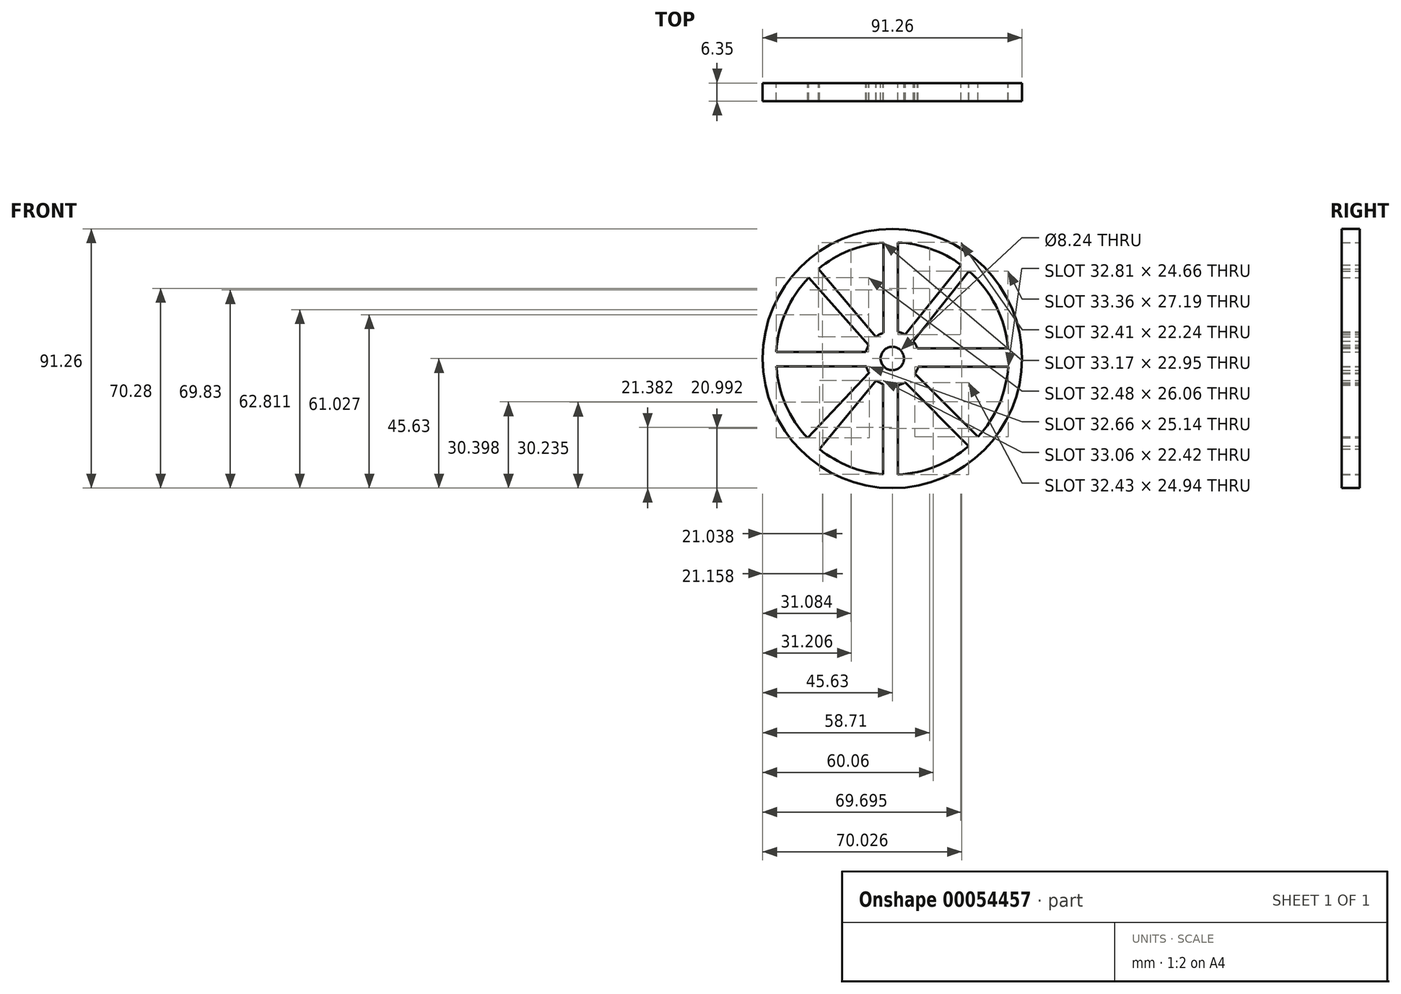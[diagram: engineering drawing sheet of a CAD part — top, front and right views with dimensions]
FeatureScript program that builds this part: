
annotation { "Feature Type Name" : "Feature", "Feature Type Description" : "" }
export const myFeature = defineFeature(function(context is Context, id is Id, definition is map)
    precondition{}
    {
        {
            var Q0;
            Q0=qCreatedBy(makeId("Front.planeOp"),FACE);
            var sketch = newSketch(context, id + "F0", { "sketchPlane" : qUnion([Q0])});
            skCircle(sketch, "E0", {"center": v(0, 0) * mm, "radius": 9.58 * mm});
            skCircle(sketch, "E1", {"center": v(0, 0) * mm, "radius": 40.9 * mm});
            skCircle(sketch, "E2", {"center": v(0, 0) * mm, "radius": 45.63 * mm});
            skLineSegment(sketch, "E3", {"start": v(-40.83, 2.36) * mm, "end": v(-9.28, 2.36) * mm});
            skLineSegment(sketch, "E4", {"start": v(8.88, 3.58) * mm, "end": v(40.74, 3.58) * mm});
            skLineSegment(sketch, "E5", {"start": v(9.13, -2.9) * mm, "end": v(40.8, -2.9) * mm});
            skLineSegment(sketch, "E6", {"start": v(-3.07, 9.07) * mm, "end": v(-3.07, 40.79) * mm});
            skLineSegment(sketch, "E7", {"start": v(1.96, 9.38) * mm, "end": v(1.96, 40.85) * mm});
            skLineSegment(sketch, "E8", {"start": v(-3.21, -9.02) * mm, "end": v(-3.21, -40.78) * mm});
            skLineSegment(sketch, "E9", {"start": v(1.96, -9.38) * mm, "end": v(1.96, -40.85) * mm});
            skLineSegment(sketch, "E10", {"start": v(-9.15, -2.82) * mm, "end": v(-40.8, -2.82) * mm});
            skLineSegment(sketch, "E11", {"start": v(-5.81, 7.61) * mm, "end": v(-26.02, 31.56) * mm});
            skLineSegment(sketch, "E12", {"start": v(-8.35, 4.7) * mm, "end": v(-29.4, 28.43) * mm});
            skLineSegment(sketch, "E13", {"start": v(4.52, 8.44) * mm, "end": v(24.2, 32.97) * mm});
            skLineSegment(sketch, "E14", {"start": v(7.38, 6.1) * mm, "end": v(26.94, 30.78) * mm});
            skLineSegment(sketch, "E15", {"start": v(8, -5.28) * mm, "end": v(30.22, -27.56) * mm});
            skLineSegment(sketch, "E16", {"start": v(4.56, -8.42) * mm, "end": v(26.9, -30.81) * mm});
            skLineSegment(sketch, "E17", {"start": v(-8.14, -5.05) * mm, "end": v(-29.85, -27.97) * mm});
            skLineSegment(sketch, "E18", {"start": v(-5.67, -7.72) * mm, "end": v(-25.64, -31.87) * mm});
            skCircle(sketch, "E19", {"center": v(0, 0) * mm, "radius": 4.12 * mm});
            skSolve(sketch);
        }
        {
            var Q0;
            Q0=makeQuery(id+"F0.imprint","IMPRINT",FACE,{"disambiguationData":[TD([[makeQuery(id+"F0.imprint","IMPRINT",EDGE,{"derivedFrom":sQuery(id+"F0.wireOp",EDGE,"E19")}),-1.0]])]});
            var Q1;
            {var subQ0=sQuery(id+"F0.wireOp",EDGE,"E6");Q1=makeQuery(id+"F0.imprint","IMPRINT",FACE,{"disambiguationData":[TD([[makeQuery(id+"F0.imprint","IMPRINT",EDGE,{"derivedFrom":subQ0}),-1.0]])]});}
            var Q2;
            {var subQ0=sQuery(id+"F0.wireOp",EDGE,"E11");Q2=makeQuery(id+"F0.imprint","IMPRINT",FACE,{"disambiguationData":[TD([[makeQuery(id+"F0.imprint","IMPRINT",EDGE,{"derivedFrom":subQ0}),1.0]])]});}
            var Q3;
            {var subQ0=sQuery(id+"F0.wireOp",EDGE,"E3");Q3=makeQuery(id+"F0.imprint","IMPRINT",FACE,{"disambiguationData":[TD([[makeQuery(id+"F0.imprint","IMPRINT",EDGE,{"derivedFrom":subQ0}),-1.0]])]});}
            var Q4;
            {var subQ0=sQuery(id+"F0.wireOp",EDGE,"E17");Q4=makeQuery(id+"F0.imprint","IMPRINT",FACE,{"disambiguationData":[TD([[makeQuery(id+"F0.imprint","IMPRINT",EDGE,{"derivedFrom":subQ0}),1.0]])]});}
            var Q5;
            {var subQ0=sQuery(id+"F0.wireOp",EDGE,"E8");Q5=makeQuery(id+"F0.imprint","IMPRINT",FACE,{"disambiguationData":[TD([[makeQuery(id+"F0.imprint","IMPRINT",EDGE,{"derivedFrom":subQ0}),1.0]])]});}
            var Q6;
            {var subQ0=sQuery(id+"F0.wireOp",EDGE,"E15");Q6=makeQuery(id+"F0.imprint","IMPRINT",FACE,{"disambiguationData":[TD([[makeQuery(id+"F0.imprint","IMPRINT",EDGE,{"derivedFrom":subQ0}),-1.0]])]});}
            var Q7;
            {var subQ0=sQuery(id+"F0.wireOp",EDGE,"E4");Q7=makeQuery(id+"F0.imprint","IMPRINT",FACE,{"disambiguationData":[TD([[makeQuery(id+"F0.imprint","IMPRINT",EDGE,{"derivedFrom":subQ0}),-1.0]])]});}
            var Q8;
            {var subQ0=sQuery(id+"F0.wireOp",EDGE,"E13");Q8=makeQuery(id+"F0.imprint","IMPRINT",FACE,{"disambiguationData":[TD([[makeQuery(id+"F0.imprint","IMPRINT",EDGE,{"derivedFrom":subQ0}),-1.0]])]});}
            var Q9;
            Q9=makeQuery(id+"F0.imprint","IMPRINT",FACE,{"disambiguationData":[TD([[makeQuery(id+"F0.imprint","IMPRINT",EDGE,{"derivedFrom":sQuery(id+"F0.wireOp",EDGE,"E2")}),1.0]])]});
            extrude(context, id + "F1", {"entities" : qUnion([Q0, Q1, Q2, Q3, Q4, Q5, Q6, Q7, Q8, Q9]), "depth" : 6.35 * mm});
        }
    });
